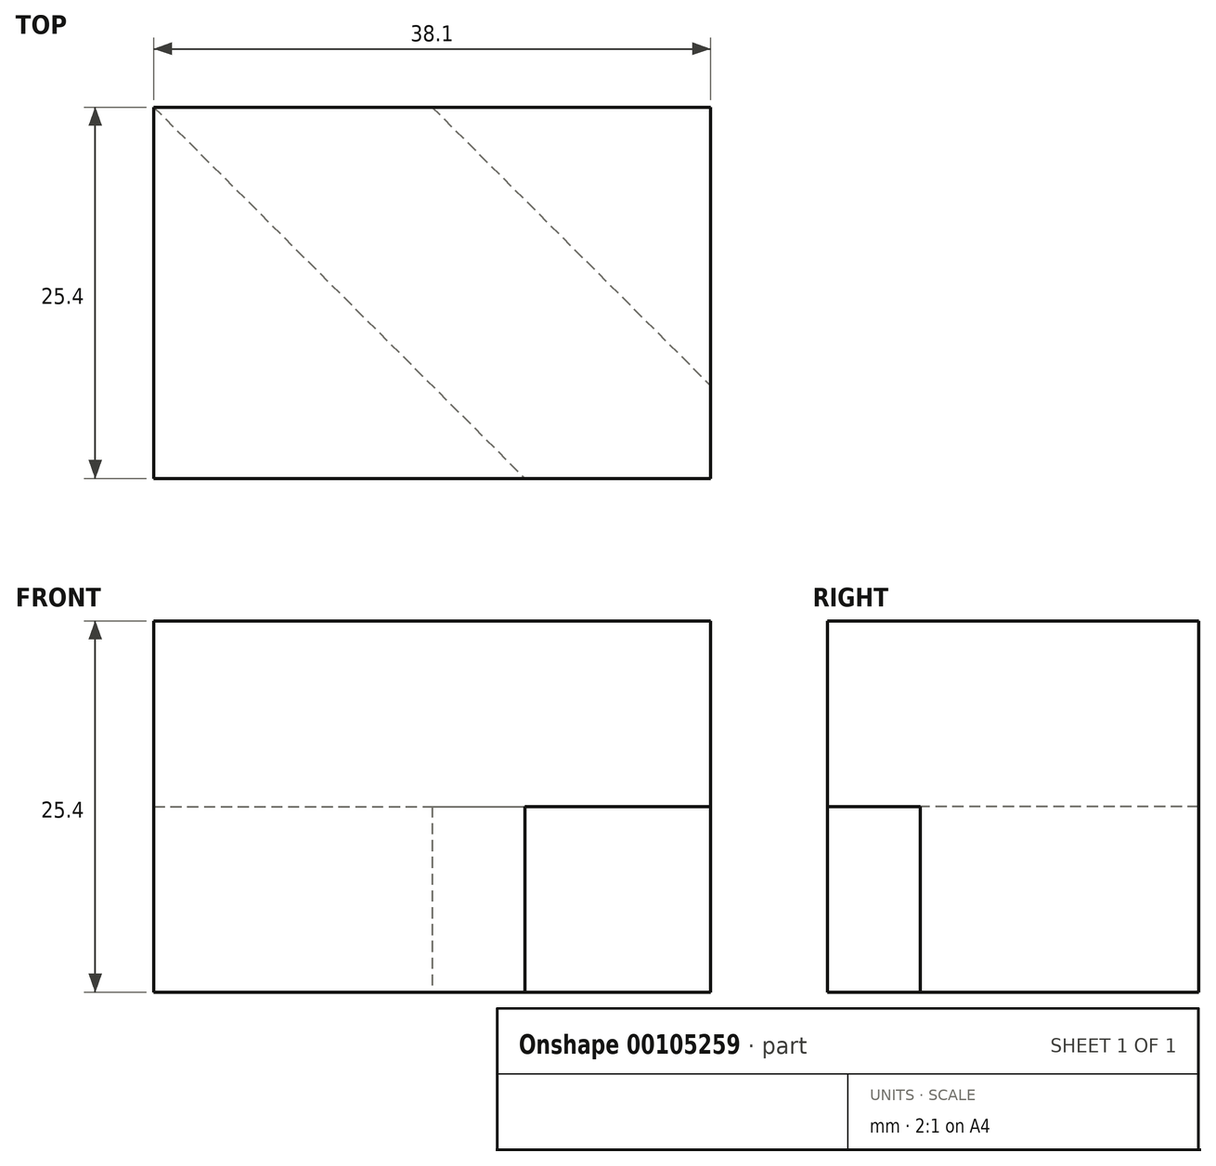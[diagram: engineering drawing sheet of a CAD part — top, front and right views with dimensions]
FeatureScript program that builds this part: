
annotation { "Feature Type Name" : "Feature", "Feature Type Description" : "" }
export const myFeature = defineFeature(function(context is Context, id is Id, definition is map)
    precondition{}
    {
        {
            var Q0;
            Q0=qCreatedBy(makeId("Front.planeOp"),FACE);
            var sketch = newSketch(context, id + "F0", { "sketchPlane" : qUnion([Q0])});
            skLineSegment(sketch, "E0", {"start": v(0, 0) * mm, "end": v(0, 25.4) * mm});
            skLineSegment(sketch, "E1", {"start": v(0, 25.4) * mm, "end": v(38.1, 25.4) * mm});
            skLineSegment(sketch, "E2", {"start": v(38.1, 25.4) * mm, "end": v(38.1, 0) * mm});
            skLineSegment(sketch, "E3", {"start": v(38.1, 0) * mm, "end": v(0, 0) * mm});
            skSolve(sketch);
        }
        {
            var Q0;
            Q0 = qSketchRegion(id + "F0", true);
            extrude(context, id + "F1", {"entities" : qUnion([Q0]), "depth" : 25.4 * mm});
        }
        {
            var Q0;
            Q0=qCreatedBy(makeId("Top.planeOp"),FACE);
            var sketch = newSketch(context, id + "F2", { "sketchPlane" : qUnion([Q0])});
            skLineSegment(sketch, "E4", {"start": v(0, 0) * mm, "end": v(25.4, -25.4) * mm});
            skLineSegment(sketch, "E5", {"start": v(19.05, 0) * mm, "end": v(38.1, -19.05) * mm});
            skLineSegment(sketch, "E6", {"start": v(0, 0) * mm, "end": v(19.05, 0) * mm});
            skLineSegment(sketch, "E7", {"start": v(38.1, -19.05) * mm, "end": v(38.1, -25.4) * mm});
            skLineSegment(sketch, "E8", {"start": v(38.1, -25.4) * mm, "end": v(25.4, -25.4) * mm});
            skSolve(sketch);
        }
        {
            var Q0;
            Q0 = qSketchRegion(id + "F2", true);
            extrude(context, id + "F3", {"entities" : qUnion([Q0]), "operationType" : NewBodyOperationType.REMOVE, "depth" : 12.7 * mm});
        }
    });
